# Revit family: SW 200i OHC Doors by Others Dual Swing Door Operators
name_source: partatom
category: Doors
revit_build: Autodesk Revit Architecture 2014 (Build: 20130308_1515(x64)
units: mm (PartAtom-declared; Revit-internal decimal feet)

## types (1)
- SW 200i OHC Doors by Others Dual Swing Door Operators
    Analytic Construction = <None>
    BIMobject category = Swing Doors
    Bottom Profile Option_01 = Leaf : 0' 04''
    Bottom Profile Option_02 = Leaf : 0' 07''
    Bottom Profile Option_03 = Leaf : 0' 10''
    Bottom Profile Option_04 = Leaf : 1' 0''
    Bottom_Profile_Height = Leaf : 0' 04''
    Brass Polished Finish = Brass, Polished
    Brass Satin Finish = Brass, Satin
    Dark Bronze Anodized = Dark Bronze Anodized
    Date of publishing = 2015-02-23
    Depth = 0.00
    Edition number = 1
    Frame Material = Aluminum
    Gap = 0' - 0 1/4"
    Glass = Glass
    Header Lenght = 6' - 9 13/16"
    Height = 6' - 11 3/4"
    IFC Classification = Door
    Jambs Thickness = 0' - 1 3/4"
    Leaf Height = 6' - 5 5/8"
    Leaf Width = 3' - 3 23/32"
    Manufacturer name = Besam-North America
    Material main = Aluminium
    Nominal height = 0.00
    Nominal width = 0.00
    Product SKU = SW200i_OHC
    Product data url = http://besam-na.bimobject.com
    Product family = Swing
    Product group = Overhead Concealed
    QR code = http://besam-na.bimobject.com
    Rough Height = 7' - 0"
    Rough Width = 7' - 2"
    Rubber = Rubber
    Stainless Steel Polished Finish = Stainless Steel, Polished
    Stainless Steel Satin Finish = Stainless Steel, Satin
    UNSPSC Code = 30171511
    Uniclass 1.4 Code = L81323
    Uniclass 1.4 Description = Swings
    Wall Closure = By host
    Weight Net (Kg) = 0
    Width = 7' - 1 1/2"

## geometry (parser evidence)
native form markers: Blend x6, Sweep x53
no freeform markers — native parametric forms only
